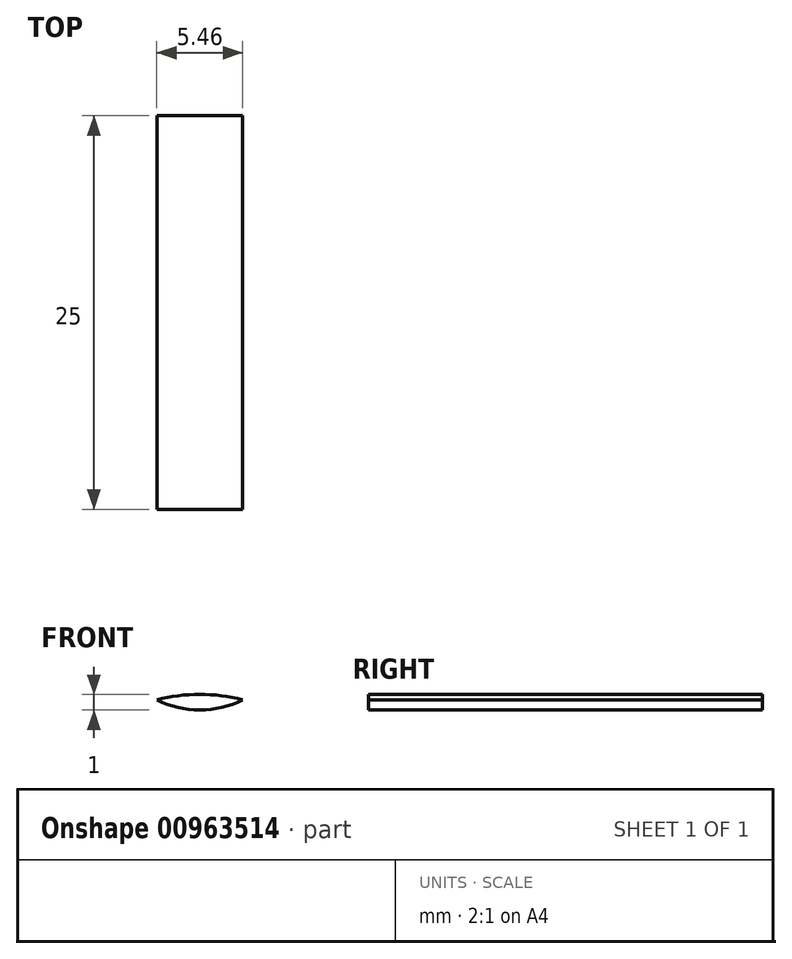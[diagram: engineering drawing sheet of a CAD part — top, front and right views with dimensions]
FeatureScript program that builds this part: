
annotation { "Feature Type Name" : "Feature", "Feature Type Description" : "" }
export const myFeature = defineFeature(function(context is Context, id is Id, definition is map)
    precondition{}
    {
        {
            var Q0;
            Q0=qCreatedBy(makeId("Front.planeOp"),FACE);
            var sketch = newSketch(context, id + "F0", { "sketchPlane" : qUnion([Q0])});
            skCircle(sketch, "E0", {"center": v(0, 0) * mm, "radius": 11 * mm});
            skCircle(sketch, "E1", {"center": v(0, 0) * mm, "radius": 12.5 * mm});
            skCircle(sketch, "E2", {"center": v(0, 16) * mm, "radius": 2.5 * mm});
            skCircle(sketch, "E3", {"center": v(0, 16) * mm, "radius": 6 * mm});
            skLineSegment(sketch, "E4", {"start": v(-5.48, 18.44) * mm, "end": v(-11.42, 5.08) * mm});
            skLineSegment(sketch, "E5", {"start": v(5.48, 18.44) * mm, "end": v(11.42, 5.08) * mm});
            skCircle(sketch, "E6", {"center": v(0, 0) * mm, "radius": 8.75 * mm});
            skSolve(sketch);
        }
        {
            var Q0;
            {var subQ0=sQuery(id+"F0.wireOp",EDGE,"E3");var subQ1=sQuery(id+"F0.wireOp",EDGE,"E0");var subQ2=makeQuery(id+"F0.imprint","INTERSECT",VERTEX,{"disambiguationData":[OD(0.0)],"derivedFrom":[subQ1,subQ0]});Q0=makeQuery(id+"F0.imprint","IMPRINT",FACE,{"disambiguationData":[TD([[makeQuery(id+"F0.imprint","IMPRINT",EDGE,{"disambiguationData":[TD([[subQ2,-1.0]])],"derivedFrom":subQ1}),1.0]])]});}
            extrude(context, id + "F1", {"entities" : qUnion([Q0]), "depth" : 25 * mm, "offsetDistance" : 25 * mm});
        }
    });
